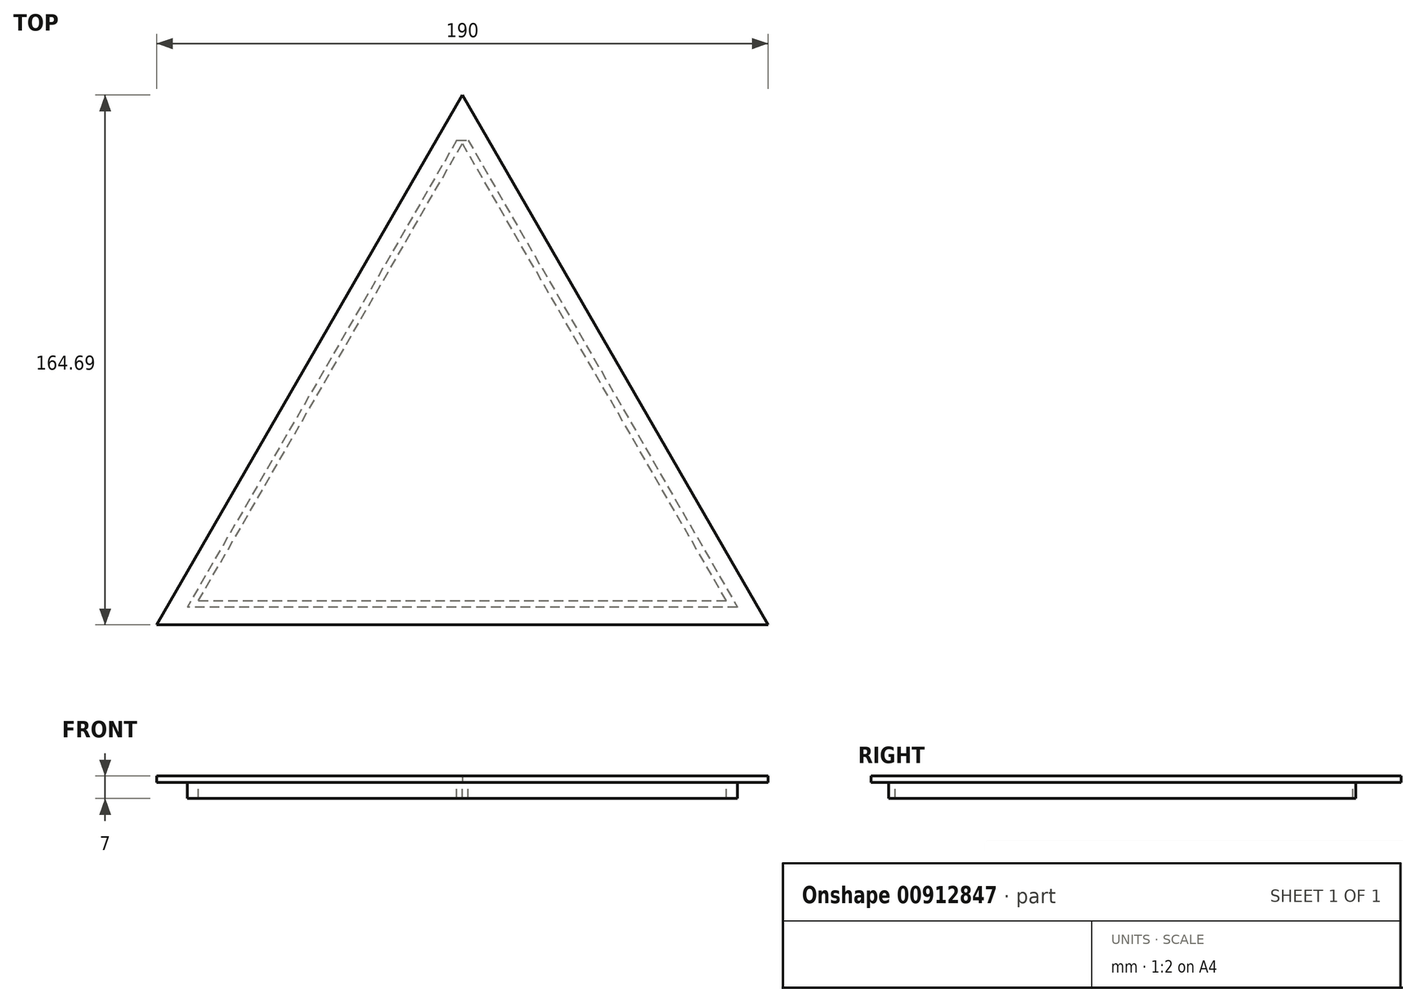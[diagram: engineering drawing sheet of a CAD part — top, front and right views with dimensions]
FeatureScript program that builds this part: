
annotation { "Feature Type Name" : "Feature", "Feature Type Description" : "" }
export const myFeature = defineFeature(function(context is Context, id is Id, definition is map)
    precondition{}
    {
        {
            var Q0;
            Q0=qCreatedBy(makeId("Top.planeOp"),FACE);
            var sketch = newSketch(context, id + "F0", { "sketchPlane" : qUnion([Q0])});
            skLineSegment(sketch, "E0", {"start": v(0, 0) * mm, "end": v(95, 0) * mm});
            skLineSegment(sketch, "E1.MirrorCS", {"start": v(0, 0) * mm, "end": v(-95, 0) * mm});
            skLineSegment(sketch, "E2", {"start": v(0, 164.69) * mm, "end": v(0, 165.72) * mm, "construction": true});
            skLineSegment(sketch, "E3", {"start": v(-95, 0) * mm, "end": v(0, 164.69) * mm});
            skLineSegment(sketch, "E4.MirrorCS", {"start": v(95, 0) * mm, "end": v(0, 164.69) * mm});
            skLineSegment(sketch, "E5", {"start": v(-86.34, 5) * mm, "end": v(-89.23, 0) * mm});
            skLineSegment(sketch, "E6", {"start": v(86.34, 5) * mm, "end": v(92.12, 5) * mm});
            skLineSegment(sketch, "E7.MirrorCS", {"start": v(86.34, 5) * mm, "end": v(89.23, 0) * mm});
            skPoint(sketch, "E8.end.orphan", {"position": v(0, 154.68) * mm});
            skPoint(sketch, "E9.MirrorCS.start.orphan", {"position": v(48.97, 69.79) * mm});
            skPoint(sketch, "E10.end.orphan", {"position": v(-48.97, 69.79) * mm});
            skLineSegment(sketch, "E11", {"start": v(0, 0) * mm, "end": v(0, 15) * mm, "construction": true});
            skLineSegment(sketch, "E12", {"start": v(-50.2, 77.67) * mm, "end": v(-37.2, 70.17) * mm, "construction": true});
            skLineSegment(sketch, "E13", {"start": v(0, 15) * mm, "end": v(-86.35, 15) * mm});
            skLineSegment(sketch, "E14", {"start": v(-37.2, 70.17) * mm, "end": v(-69.03, 15) * mm});
            skLineSegment(sketch, "E15", {"start": v(-37.2, 70.17) * mm, "end": v(0, 134.67) * mm});
            skLineSegment(sketch, "E16.MirrorCS", {"start": v(0, 15) * mm, "end": v(86.35, 15) * mm});
            skLineSegment(sketch, "E17.MirrorCS", {"start": v(37.2, 70.17) * mm, "end": v(69.03, 15) * mm});
            skLineSegment(sketch, "E18.MirrorCS", {"start": v(37.2, 70.17) * mm, "end": v(0, 134.67) * mm});
            skSolve(sketch);
        }
        {
            var Q0;
            {var subQ3=sQuery(id+"F0.wireOp",EDGE,"E14");Q0=makeQuery(id+"F0.imprint","IMPRINT",FACE,{"disambiguationData":[TD([[makeQuery(id+"F0.imprint","IMPRINT",EDGE,{"derivedFrom":subQ3}),-1.0]])]});}
            var Q1;
            {var subQ5=sQuery(id+"F0.wireOp",EDGE,"E6");Q1=makeQuery(id+"F0.imprint","IMPRINT",FACE,{"disambiguationData":[TD([[makeQuery(id+"F0.imprint","IMPRINT",EDGE,{"derivedFrom":subQ5}),1.0]])]});}
            var Q2;
            {var subQ4=sQuery(id+"F0.wireOp",EDGE,"E6");Q2=makeQuery(id+"F0.imprint","IMPRINT",FACE,{"disambiguationData":[TD([[makeQuery(id+"F0.imprint","IMPRINT",EDGE,{"derivedFrom":subQ4}),-1.0]])]});}
            var Q3;
            {var subQ4=sQuery(id+"F0.wireOp",EDGE,"E14");Q3=makeQuery(id+"F0.imprint","IMPRINT",FACE,{"disambiguationData":[TD([[makeQuery(id+"F0.imprint","IMPRINT",EDGE,{"derivedFrom":subQ4}),1.0]])]});}
            extrude(context, id + "F1", {"entities" : qUnion([Q0, Q1, Q2, Q3]), "depth" : 2 * mm, "offsetDistance" : 25 * mm});
        }
        {
            var Q0;
            Q0=makeQuery(id+"F1.opExtrude","CAP_FACE",FACE,{"disambiguationData":[OSD([sQuery(id+"F0.wireOp",EDGE,"E0"),sQuery(id+"F0.wireOp",EDGE,"E1.MirrorCS"),sQuery(id+"F0.wireOp",EDGE,"E3"),sQuery(id+"F0.wireOp",EDGE,"E4.MirrorCS"),sQuery(id+"F0.wireOp",EDGE,"E13"),sQuery(id+"F0.wireOp",EDGE,"E14"),sQuery(id+"F0.wireOp",EDGE,"E15"),sQuery(id+"F0.wireOp",EDGE,"E16.MirrorCS"),sQuery(id+"F0.wireOp",EDGE,"E17.MirrorCS"),sQuery(id+"F0.wireOp",EDGE,"E18.MirrorCS")])],"isStart":true});
            var sketch = newSketch(context, id + "F2", { "sketchPlane" : qUnion([Q0])});
            skLineSegment(sketch, "E19", {"start": v(57.37, -65.23) * mm, "end": v(44.38, -57.74) * mm});
            skLineSegment(sketch, "E20", {"start": v(44.38, -57.74) * mm, "end": v(50.87, -61.48) * mm});
            skLineSegment(sketch, "E21", {"start": v(50.87, -61.48) * mm, "end": v(83.17, -5.5) * mm});
            skLineSegment(sketch, "E22", {"start": v(50.87, -61.48) * mm, "end": v(0, -149.68) * mm});
            skLineSegment(sketch, "E23", {"start": v(1.73, -150.67) * mm, "end": v(85.48, -5.5) * mm});
            skLineSegment(sketch, "E24.MirrorCS", {"start": v(-50.87, -61.48) * mm, "end": v(-83.17, -5.5) * mm});
            skLineSegment(sketch, "E25.MirrorCS", {"start": v(-50.87, -61.48) * mm, "end": v(0, -149.68) * mm});
            skLineSegment(sketch, "E26.MirrorCS", {"start": v(-1.73, -150.67) * mm, "end": v(-85.48, -5.5) * mm});
            skLineSegment(sketch, "E27", {"start": v(-1.73, -150.67) * mm, "end": v(1.73, -150.67) * mm});
            skLineSegment(sketch, "E28", {"start": v(0, -7.5) * mm, "end": v(82.02, -7.5) * mm});
            skLineSegment(sketch, "E29", {"start": v(0, -7.5) * mm, "end": v(-82.02, -7.5) * mm});
            skPoint(sketch, "E30.orphan", {"position": v(0, -15) * mm});
            skPoint(sketch, "E31.start.orphan", {"position": v(0, 0) * mm});
            skLineSegment(sketch, "E32", {"start": v(-12.32, -7.5) * mm, "end": v(-12.32, -5.5) * mm, "construction": true});
            skLineSegment(sketch, "E33", {"start": v(-12.32, -5.5) * mm, "end": v(-83.17, -5.5) * mm});
            skLineSegment(sketch, "E34", {"start": v(-12.32, -5.5) * mm, "end": v(83.17, -5.5) * mm});
            skLineSegment(sketch, "E35", {"start": v(-83.17, -5.5) * mm, "end": v(-85.48, -5.5) * mm});
            skLineSegment(sketch, "E36", {"start": v(83.17, -5.5) * mm, "end": v(85.48, -5.5) * mm});
            skPoint(sketch, "E37.orphan", {"position": v(-86.34, 0) * mm});
            skPoint(sketch, "E38.orphan", {"position": v(-88.65, 0) * mm});
            skPoint(sketch, "E39.orphan", {"position": v(86.34, 0) * mm});
            skPoint(sketch, "E40.orphan", {"position": v(88.65, 0) * mm});
            skSolve(sketch);
        }
        {
            var Q0;
            {var subQ8=sQuery(id+"F2.wireOp",EDGE,"E22");Q0=makeQuery(id+"F2.imprint","IMPRINT",FACE,{"disambiguationData":[TD([[makeQuery(id+"F2.imprint","IMPRINT",EDGE,{"derivedFrom":subQ8}),1.0]])]});}
            var Q1;
            {var subQ0=sQuery(id+"F2.wireOp",EDGE,"E28");Q1=makeQuery(id+"F2.imprint","IMPRINT",FACE,{"disambiguationData":[TD([[makeQuery(id+"F2.imprint","IMPRINT",EDGE,{"derivedFrom":subQ0}),1.0]])]});}
            var Q2;
            {var subQ0=sQuery(id+"F2.wireOp",EDGE,"E36");Q2=makeQuery(id+"F2.imprint","IMPRINT",FACE,{"disambiguationData":[TD([[makeQuery(id+"F2.imprint","IMPRINT",EDGE,{"derivedFrom":subQ0}),-1.0]])]});}
            extrude(context, id + "F3", {"entities" : qUnion([Q0, Q1, Q2]), "operationType" : NewBodyOperationType.ADD, "depth" : 5 * mm, "offsetDistance" : 25 * mm});
        }
    });
